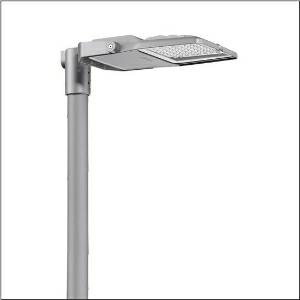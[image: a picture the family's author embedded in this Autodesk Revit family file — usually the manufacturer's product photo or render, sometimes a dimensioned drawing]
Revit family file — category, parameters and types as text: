
# Revit family: floodlight_fl_21_iq_mini___pl52_5xa7771c2d3a_33da
name_source: partatom
category: Lighting Fixtures
units: mm (PartAtom-declared; Revit-internal decimal feet)

## family parameters
Cut with Voids When Loaded = No
Host = Face
Light Source = No
Part Type = Normal
Room Calculation Point = No
Round Connector Dimension = Use Diameter
Shared = No

## types (1)
- --- (1 x LED, 12210 lm, 87.2 W, 3000K)
    Apparent Load = 87 VA
    CIE Flux Codes = 26 60 98 100 100
    Color Rendering = 70
    Color Temperature = 3000K
    Default Elevation = 1800 mm
    Description = Floodlight FL 21 iQ mini, floodlight, primary light control with lens, of PMMA, primary optical cover: protective disc, of toughened safety glass, transparent, light distribution: PL52, light emission: direct distribution, installation type: surface-mounted, lamps: LED, High Power LED, rated values: 12.210lm | 87,2W | 140lm/W (begin service life); end service life: 12.210lm | 92,1W; at 50% lumin. flux: 6.105lm | 40,1W | 152,2lm/W, colour temperature: 3000K, colour rendering: CRI > 70, light colour: 730, light setting 1 begin service life: 100% | 12.210lm | 87,2W | 140lm/W | 3.000K, light setting 1 end service life: 92,1W, further light settings possible, control: Auto-Match, Temp-Guard, Lumen-Switch, Night-Set, Smart-Wire, Light-Fading, Desk-Remote (wireless, voltage-free reading and setting of iQ features in the workshop via application-optimized NFC function/RFID function), optimised constant luminous flux control (CLO 2.0), pre-setting: linear dimming characteristic, with terminal, 6-pole, mains connection: 220..240V, AC, 50/60Hz, luminaire housing, of diecast aluminium, powder-coated, SITECO metallic grey (DB 702S), corrosivity category C5 mid according to DIN EN ISO 12944suitable for swimming poolschlorine-resistant, sealing non-destructively replaceable, please order mast flange separately, mast bracket, of steel, galvanised, powder-coated, SITECO metallic grey (DB 702S), protection rating (complete): IP66, insulation class (complete): insulation class II (safety insulation), certification: CE, ENEC, VDE, protection symbol: D, impact resistance: IK08, permissible operating ambient temperature: -40..+40°C, permissible operating ambient temperature for outdoor applications: -40..+50°C, standard: DIN EN 12944, LABS conformity tested according to VDMA 24364:2018-05, packaging unit: 1 piece

Light Distribution: PL52
    Height = 70 mm
    Lamp = 1 x LED
    Lamp Light Flux = 12210 lm
    Lamp Power = 87.2 W
    Lamp count = 1
    Length = 485 mm
    Luminous efficacy = 140 lm/W
    Manufacturer = Siteco
    ModVariant = No
    Model = 5XA7771C2D3A
    Number of Poles = 1
    OnlyDefault = Yes
    Power Factor = 1
    Product Name = Floodlight FL 21 iQ mini | PL52
    Product group = floodlight | pylon annexe
    ProductGroupID = 6201
    Protection Class = Protection class II
    Protection Degree = IP 66
    RLX_Detail_Level = 1
    RLX_Emergency_Light_Flux = 0 lm
    RLX_Emergency_Type = 0
    RLX_Emergency_Type_DB = No
    RlxData = <blob elided: 101789 chars, md5=1d398040>
    Socket = socket
    Standby Power = 0 W
    System Light Flux = 12210 lm
    System Power = 87 W
    Type Comments = factory setting: luminous flux: 100 % | dim-lin: 254 | 456 mA
    Type Image = l_1007125.jpg
    URL = http://relux.com
    VarID = @adj_164025
    Voltage = 0 V
    Weight = 0.00 kg
    Width = 337 mm

## geometry (parser evidence)
native form markers: Blend x4, Sweep x11
no freeform markers — native parametric forms only
